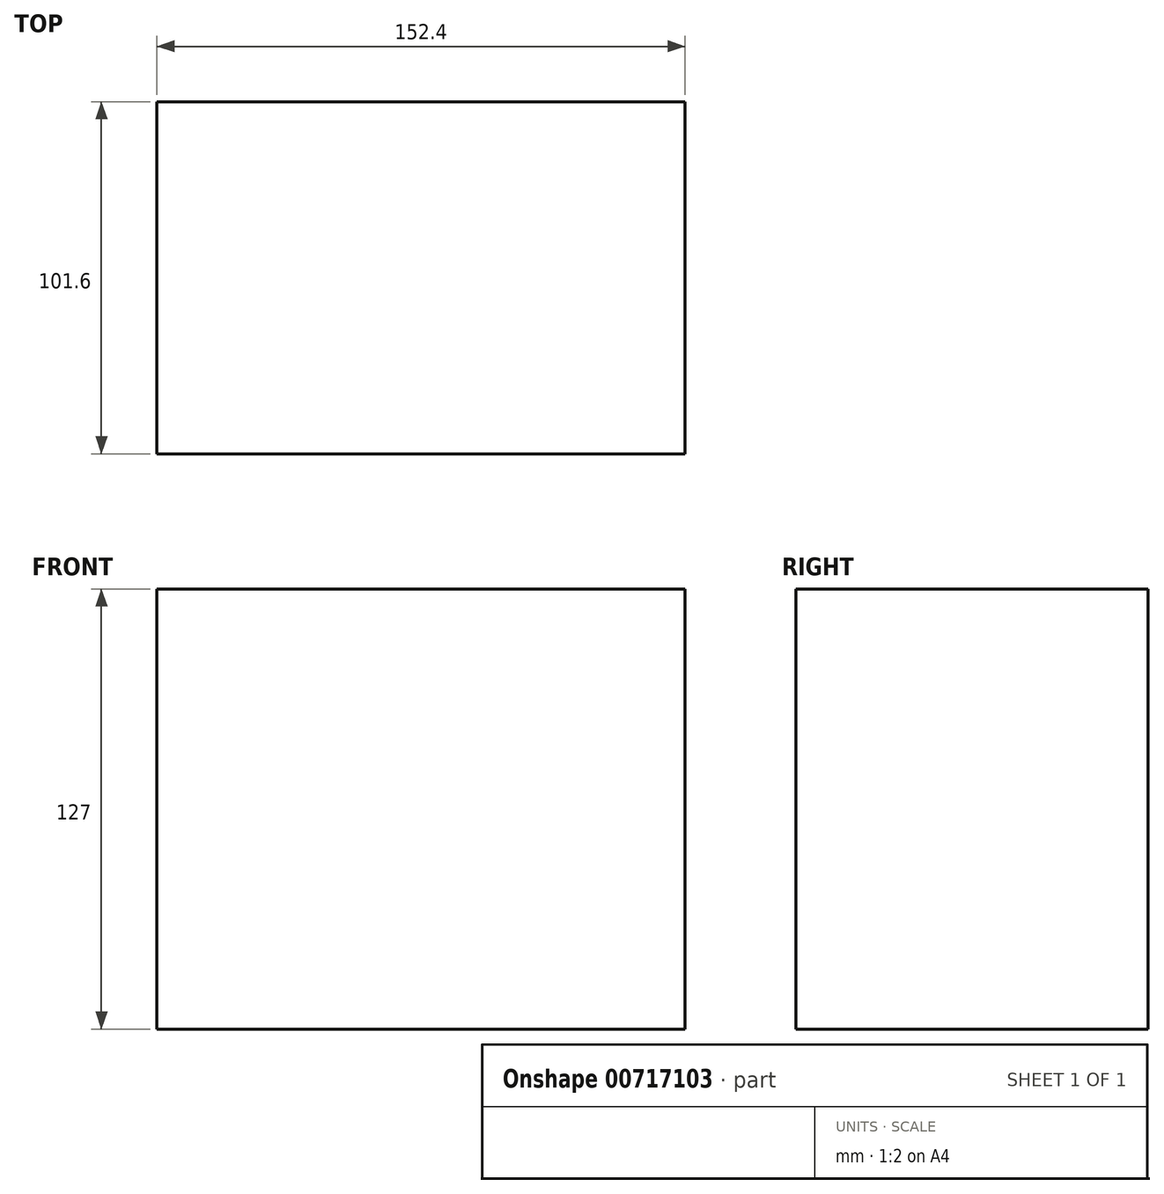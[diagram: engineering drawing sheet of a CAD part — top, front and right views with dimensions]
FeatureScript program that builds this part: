
annotation { "Feature Type Name" : "Feature", "Feature Type Description" : "" }
export const myFeature = defineFeature(function(context is Context, id is Id, definition is map)
    precondition{}
    {
        {
            var Q0;
            Q0=qCreatedBy(makeId("Front.planeOp"),FACE);
            var sketch = newSketch(context, id + "F0", { "sketchPlane" : qUnion([Q0])});
            skLineSegment(sketch, "E0", {"start": v(-125.7, 85.97) * mm, "end": v(-125.7, -41.03) * mm});
            skLineSegment(sketch, "E1", {"start": v(-125.7, -41.03) * mm, "end": v(26.7, -41.03) * mm});
            skLineSegment(sketch, "E2", {"start": v(26.7, -41.03) * mm, "end": v(26.7, 85.97) * mm});
            skLineSegment(sketch, "E3", {"start": v(26.7, 85.97) * mm, "end": v(-125.7, 85.97) * mm});
            skSolve(sketch);
        }
        {
            var Q0;
            Q0=makeQuery(id+"F0.imprint","IMPRINT",FACE,{"disambiguationData":[TD([[makeQuery(id+"F0.imprint","IMPRINT",EDGE,{"derivedFrom":sQuery(id+"F0.wireOp",EDGE,"E0")}),1.0]])]});
            extrude(context, id + "F1", {"entities" : qUnion([Q0]), "depth" : 101.6 * mm, "offsetDistance" : 25.4 * mm});
        }
    });
